# Revit family: Shower-Shower_Panel-KOHLER-Real_Rain-K-31110_1
name_source: partatom
category: Plumbing Fixtures
revit_build: Autodesk Revit 2017 (Build: 20160225_1515(x64)
units: mm (PartAtom-declared; Revit-internal decimal feet)

## family parameters
Cut with Voids When Loaded = No
Host = Face
OmniClass Number = 23.31.17.00
OmniClass Title = Showers
Part Type = Normal
Room Calculation Point = No
Round Connector Dimension = Use Diameter
Shared = No

## types (4) — shared parameters
ADA Compliant = No
Assembly Code = D2010700
CW Connection = No
Cold Water Inlet = Cold Water Inlet
Date Modified = 02/16/2021
Default Elevation = 0"
Description = Overhead Panel
Drain Included = No
HW Connection = Yes
Height = 4 11/16"
Hot Water Inlet = Tempered Water Inlet
Length = 19 3/16"
Manufacturer = KOHLER Co.
Master Format 2014 = 22 42 23
Master Format 2014 Name = Residential Showers
Material = Silicone
Panel Thickness = 11/16"
Product Documentation Link = https://www.us.kohler.com
Product Name = Real Rain
Product Page URL = http://www.us.kohler.com
URL = https://www.us.kohler.com
Vent Connection = No
Waste Connection = No
Waste Water Outlet = Waste Water Outlet
WaterSense Certified = No
Width = 19 3/16"

## per-type parameters (varying)
| type | Finish | Flow Rate | Model | Pressure | Type |
| 2.5 GPM, 0- White | Kohler-Silicone-0-White | 3 GPM | K-31110-0 | 40.00 psi | 1 |
| 2.5 GPM, 58- Thunder Grey | Kohler-Silicone-58-Thunder_Grey | 3 GPM | K-31110-58 | 40.00 psi | 2 |
| 1.75 GPM, 0- White | Kohler-Silicone-0-White | 2 GPM | K-31110-G-0 | 80.00 psi | 3 |
| 1.75 GPM, 58- Thunder Grey | Kohler-Silicone-58-Thunder_Grey | 2 GPM | K-31110-G-58 | 80.00 psi | 4 |

## geometry (parser evidence)
native form markers: Sweep x5
no freeform markers — native parametric forms only
